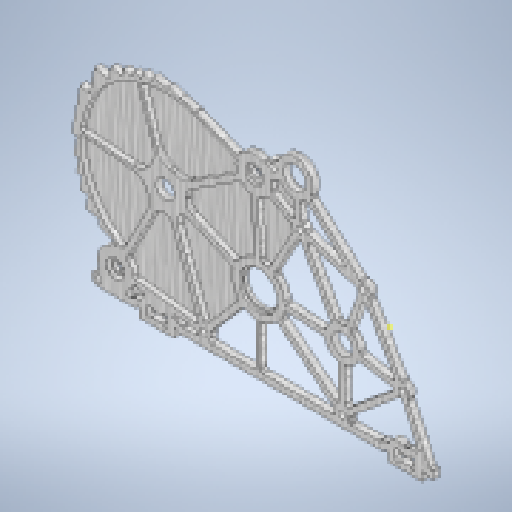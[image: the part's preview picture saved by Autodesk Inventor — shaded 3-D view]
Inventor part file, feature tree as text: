
AUTODESK INVENTOR PART (.ipt)
format: ipt  version: 2023 (Build 270158000, 158)  size: 5,919,744 bytes
history: native  units: mm
features: sketch x37, extrude x35, other x19, fillet x15, projected_geometry x13, hole x5
ambient origin geometry x8: Origin, YZ Plane, XZ Plane, XY Plane, X Axis, Y Axis, Z Axis, Center Point
bodies: Body1 (feature_tree)
feature tree (124):
  other  "ソリッド1"
  sketch  "スケッチ1"
  sketch  "スケッチ2"
  extrude  "押し出し1"  Depth=0.95mm
  sketch  "スケッチ3"
  hole  "穴1"  [1 undecoded]
  hole  "穴2"  [1 undecoded]
  hole  "穴3"  [1 undecoded]
  extrude  "押し出し2"  Depth=6.0mm
  extrude  "押し出し3"  Depth=6.0mm
  sketch  "スケッチ6"
  extrude  "押し出し4"  Depth=12.0mm
  extrude  "押し出し5"  Depth=1.0mm
  extrude  "押し出し6"  Depth=3.0mm
  fillet  "フィレット1"  Radius=8.05mm
  extrude  "押し出し7"  Depth=15.0mm
  fillet  "フィレット2"  Radius=9.0mm
  extrude  "押し出し8"  Depth=5.0mm
  extrude  "押し出し9"  Depth=4.0mm
  sketch  "スケッチ12"
  extrude  "押し出し10"  Depth=3.0mm
  extrude  "押し出し11"  Depth=16.0mm
  fillet  "フィレット3"  Radius=16.0mm
  sketch  "スケッチ13"
  extrude  "押し出し12"  Depth=16.0mm
  sketch  "スケッチ15"
  extrude  "押し出し13"  Depth=16.0mm
  hole  "穴4"  [1 undecoded]
  extrude  "押し出し14"  Depth=2.6mm
  fillet  "フィレット4"  Radius=2.6mm
  sketch  "スケッチ17"
  extrude  "押し出し15"  Depth=2.6mm
  sketch  "スケッチ19"
  sketch  "スケッチ20"
  extrude  "押し出し16"  Depth=2.6mm
  hole  "穴5"  [1 undecoded]
  sketch  "スケッチ21"
  extrude  "押し出し17"  Depth=2.6mm
  extrude  "押し出し18"  Depth=2.6mm
  fillet  "フィレット5"  Radius=10.5mm
  sketch  "スケッチ22"
  extrude  "押し出し19"  Depth=10.5mm
  extrude  "押し出し20"  Depth=10.5mm
  extrude  "押し出し21"  Depth=10.5mm
  fillet  "フィレット6"  Radius=3.0mm
  sketch  "スケッチ24"
  extrude  "押し出し22"  Depth=3.0mm
  extrude  "押し出し23"  Depth=3.0mm
  fillet  "フィレット7"  Radius=3.0mm
  extrude  "押し出し24"  Depth=3.0mm
  fillet  "フィレット8"  Radius=3.0mm
  sketch  "スケッチ26"
  extrude  "押し出し25"  Depth=3.0mm
  extrude  "押し出し26"  Depth=3.0mm
  fillet  "フィレット9"  Radius=1.0mm
  sketch  "スケッチ27"
  extrude  "押し出し27"  Depth=1.0mm
  extrude  "押し出し28"  Depth=3.0mm
  extrude  "押し出し29"  Depth=3.0mm
  extrude  "押し出し30"  Depth=3.0mm
  extrude  "押し出し31"  Depth=15.0mm
  sketch  "スケッチ33"
  sketch  "スケッチ34"
  sketch  "スケッチ35"
  extrude  "押し出し32"  Depth=3.0mm
  extrude  "押し出し33"  Depth=15.0mm
  fillet  "フィレット10"  Radius=3.0mm
  fillet  "フィレット11"  Radius=3.0mm
  fillet  "フィレット12"  Radius=3.0mm
  fillet  "フィレット13"  Radius=3.0mm
  fillet  "フィレット14"  Radius=3.0mm
  fillet  "フィレット15"  Radius=3.0mm
  extrude  "押し出し34"  Depth=10.0mm TaperAngle=0.0deg
  extrude  "押し出し35"  Depth=41.0mm
  sketch  "スケッチ4"
  sketch  "スケッチ5"
  sketch  "スケッチ7"
  sketch  "スケッチ8"
  sketch  "スケッチ9"
  sketch  "スケッチ10"
  sketch  "スケッチ11"
  sketch  "スケッチ14"
  projected_geometry  "投影ループ1"
  sketch  "スケッチ16"
  projected_geometry  "投影ループ2"
  sketch  "スケッチ18"
  projected_geometry  "投影ループ3"
  projected_geometry  "投影ループ4"
  projected_geometry  "投影ループ5"
  projected_geometry  "投影ループ6"
  sketch  "スケッチ23"
  projected_geometry  "投影ループ7"
  projected_geometry  "投影ループ8"
  sketch  "スケッチ25"
  projected_geometry  "投影ループ9"
  projected_geometry  "投影ループ10"
  projected_geometry  "投影ループ11"
  sketch  "スケッチ28"
  sketch  "スケッチ29"
  sketch  "スケッチ30"
  projected_geometry  "投影ループ12"
  sketch  "スケッチ31"
  projected_geometry  "投影ループ13"
  sketch  "スケッチ32"
  sketch  "スケッチ36"
  sketch  "スケッチ37"
  other  "断面エッジを投影1"
  other  "断面エッジを投影2"
  other  "断面エッジを投影3"
  other  "断面エッジを投影4"
  other  "断面エッジを投影5"
  other  "断面エッジを投影6"
  other  "断面エッジを投影7"
  other  "断面エッジを投影8"
  other  "断面エッジを投影9"
  other  "断面エッジを投影10"
  other  "断面エッジを投影11"
  other  "断面エッジを投影12"
  other  "断面エッジを投影13"
  other  "断面エッジを投影14"
  other  "断面エッジを投影15"
  other  "断面エッジを投影16"
  other  "断面エッジを投影17"
  other  "断面エッジを投影18"
note: 5 required parameter values undecoded (feature->parameter linkage not recoverable at this tier; creation-order binding heuristic only, values carry confidence <= 0.55)
